# Revit family: Haworth_Compose_Worksurface_Rectangular
name_source: partatom
category: Furniture Systems
revit_build: Autodesk Revit 2018 (Build: 20170223_1515(x64)
units: mm (PartAtom-declared; Revit-internal decimal feet)

## family parameters
Always vertical = Yes
Cut with Voids When Loaded = No
OmniClass Number = 23.40.70.14.64.21
OmniClass Title = Systems Furniture
Part Type = Normal
Room Calculation Point = No
Round Connector Dimension = Use Diameter
Shared = No
Work Plane-Based = No

## types (99) — shared parameters
Actual Height = 29"
Assembly Code = E2020200
Cantilever Bracket = Yes
Cantilever Bracket Location = 1 3/4"
Description = Haworth - Worksurface - Compose Rectangular
Double Support Leg = No
End Support Location = 1 3/4"
Height = 29"
Manufacturer = Haworth
Max. Depth = 36"
Max. Height = 48"
Max. Width = 120"
Min. Depth = 18"
Min. Height = 24"
Min. Width = 24"
Min/Max Depth = 18-36 in.
Min/Max Height = 26-32 in.
Min/Max Width = 24-120 in.
Model = WURA
Revision Number = 5
Size = Verify Final Dim. w/ Haworth
Support Column = No
Support Finish = Haworth _ Paint _ Metallic Champagne
Support Height = 27 13/16"
Support P Leg = No
Support Panel = No
Support Post_45 Degree = No
Support Post_90 Degree = No
Sustainability Info = http://media.haworth.com
Table Thickness = 1 3/16"
URL = www.haworth.com
URL - Product = http://www.haworth.com
Warranty = http://www.haworth.com
Worksurface Edge Finish = Haworth _ Laminate _ Maple H-AE
Worksurface Finish = Haworth _ Laminate _ Maple H-AE

## per-type parameters (varying)
| type | Actual Depth | Actual Width | Custom Size | Depth | Width |
| 24w 18d | 18" | 24" | No | 18" | 24" |
| 27w 18d | 18" | 27" | Yes | 18" | 27" |
| 30w 18d | 18" | 30" | No | 18" | 30" |
| 33w 18d | 18" | 33" | Yes | 18" | 33" |
| 36w 18d | 18" | 36" | No | 18" | 36" |
| 39w 18d | 18" | 39" | Yes | 18" | 39" |
| 42w 18d | 18" | 42" | No | 18" | 42" |
| 45w 18d | 18" | 45" | Yes | 18" | 45" |
| 48w 18d | 18" | 48" | No | 18" | 48" |
| 51w 18d | 18" | 51" | Yes | 18" | 51" |
| 54w 18d | 18" | 54" | No | 18" | 54" |
| 57w 18d | 18" | 57" | Yes | 18" | 57" |
| 60w 18d | 18" | 60" | No | 18" | 60" |
| 63w 18d | 18" | 63" | Yes | 18" | 63" |
| 66w 18d | 18" | 66" | No | 18" | 66" |
| 69w 18d | 18" | 69" | Yes | 18" | 69" |
| 72w 18d | 18" | 72" | No | 18" | 72" |
| 75w 18d | 18" | 75" | Yes | 18" | 75" |
| 78w 18d | 18" | 78" | No | 18" | 78" |
| 81w 18d | 18" | 81" | Yes | 18" | 81" |
| 84w 18d | 18" | 84" | No | 18" | 84" |
| 87w 18d | 18" | 87" | Yes | 18" | 87" |
| 90w 18d | 18" | 90" | No | 18" | 90" |
| 93w 18d | 18" | 93" | Yes | 18" | 93" |
| 96w 18d | 18" | 96" | No | 18" | 96" |
| 99w 18d | 18" | 99" | Yes | 18" | 99" |
| 102w 18d | 18" | 102" | No | 18" | 102" |
| 105w 18d | 18" | 105" | Yes | 18" | 105" |
| 108w 18d | 18" | 108" | No | 18" | 108" |
| 111w 18d | 18" | 111" | Yes | 18" | 111" |
| 114w 18d | 18" | 114" | No | 18" | 114" |
| 117w 18d | 18" | 117" | Yes | 18" | 117" |
| 120w 18d | 18" | 120" | No | 18" | 120" |
| 24w 24d | 24" | 24" | No | 24" | 24" |
| 27w 24d | 24" | 27" | Yes | 24" | 27" |
| 30w 24d | 24" | 30" | No | 24" | 30" |
| 33w 24d | 24" | 33" | Yes | 24" | 33" |
| 36w 24d | 24" | 36" | No | 24" | 36" |
| 39w 24d | 24" | 39" | Yes | 24" | 39" |
| 42w 24d | 24" | 42" | No | 24" | 42" |
| 45w 24d | 24" | 45" | Yes | 24" | 45" |
| 48w 24d | 24" | 48" | No | 24" | 48" |
| 51w 24d | 24" | 51" | Yes | 24" | 51" |
| 54w 24d | 24" | 54" | No | 24" | 54" |
| 57w 24d | 24" | 57" | Yes | 24" | 57" |
| 60w 24d | 24" | 60" | No | 24" | 60" |
| 63w 24d | 24" | 63" | Yes | 24" | 63" |
| 66w 24d | 24" | 66" | No | 24" | 66" |
| 69w 24d | 24" | 69" | Yes | 24" | 69" |
| 72w 24d | 24" | 72" | No | 24" | 72" |
| 75w 24d | 24" | 75" | Yes | 24" | 75" |
| 78w 24d | 24" | 78" | No | 24" | 78" |
| 81w 24d | 24" | 81" | Yes | 24" | 81" |
| 84w 24d | 24" | 84" | No | 24" | 84" |
| 87w 24d | 24" | 87" | Yes | 24" | 87" |
| 90w 24d | 24" | 90" | No | 24" | 90" |
| 93w 24d | 24" | 93" | Yes | 24" | 93" |
| 96w 24d | 24" | 96" | No | 24" | 96" |
| 99w 24d | 24" | 99" | Yes | 24" | 99" |
| 102w 24d | 24" | 102" | No | 24" | 102" |
| 105w 24d | 24" | 105" | Yes | 24" | 105" |
| 108w 24d | 24" | 108" | No | 24" | 108" |
| 111w 24d | 24" | 111" | Yes | 24" | 111" |
| 114w 24d | 24" | 114" | No | 24" | 114" |
| 117w 24d | 24" | 117" | Yes | 24" | 117" |
| 120w 24d | 24" | 120" | No | 24" | 120" |
| 24w 30d | 30" | 24" | No | 30" | 24" |
| 27w 30d | 30" | 27" | Yes | 30" | 27" |
| 30w 30d | 30" | 30" | No | 30" | 30" |
| 33w 30d | 30" | 33" | Yes | 30" | 33" |
| 36w 30d | 30" | 36" | No | 30" | 36" |
| 39w 30d | 30" | 39" | Yes | 30" | 39" |
| 42w 30d | 30" | 42" | No | 30" | 42" |
| 45w 30d | 30" | 45" | Yes | 30" | 45" |
| 48w 30d | 30" | 48" | No | 30" | 48" |
| 51w 30d | 30" | 51" | Yes | 30" | 51" |
| 54w 30d | 30" | 54" | No | 30" | 54" |
| 57w 30d | 30" | 57" | Yes | 30" | 57" |
| 60w 30d | 30" | 60" | No | 30" | 60" |
| 63w 30d | 30" | 63" | Yes | 30" | 63" |
| 66w 30d | 30" | 66" | No | 30" | 66" |
| 69w 30d | 30" | 69" | Yes | 30" | 69" |
| 72w 30d | 30" | 72" | No | 30" | 72" |
| 75w 30d | 30" | 75" | Yes | 30" | 75" |
| 78w 30d | 30" | 78" | No | 30" | 78" |
| 81w 30d | 30" | 81" | Yes | 30" | 81" |
| 84w 30d | 30" | 84" | No | 30" | 84" |
| 87w 30d | 30" | 87" | Yes | 30" | 87" |
| 90w 30d | 30" | 90" | No | 30" | 90" |
| 93w 30d | 30" | 93" | Yes | 30" | 93" |
| 96w 30d | 30" | 96" | No | 30" | 96" |
| 99w 30d | 30" | 99" | Yes | 30" | 99" |
| 102w 30d | 30" | 102" | No | 30" | 102" |
| 105w 30d | 30" | 105" | Yes | 30" | 105" |
| 108w 30d | 30" | 108" | No | 30" | 108" |
| 111w 30d | 30" | 111" | Yes | 30" | 111" |
| 114w 30d | 30" | 114" | No | 30" | 114" |
| 117w 30d | 30" | 117" | Yes | 30" | 117" |
| 120w 30d | 30" | 120" | No | 30" | 120" |

## geometry (parser evidence)
native form markers: Sweep x12
no freeform markers — native parametric forms only
